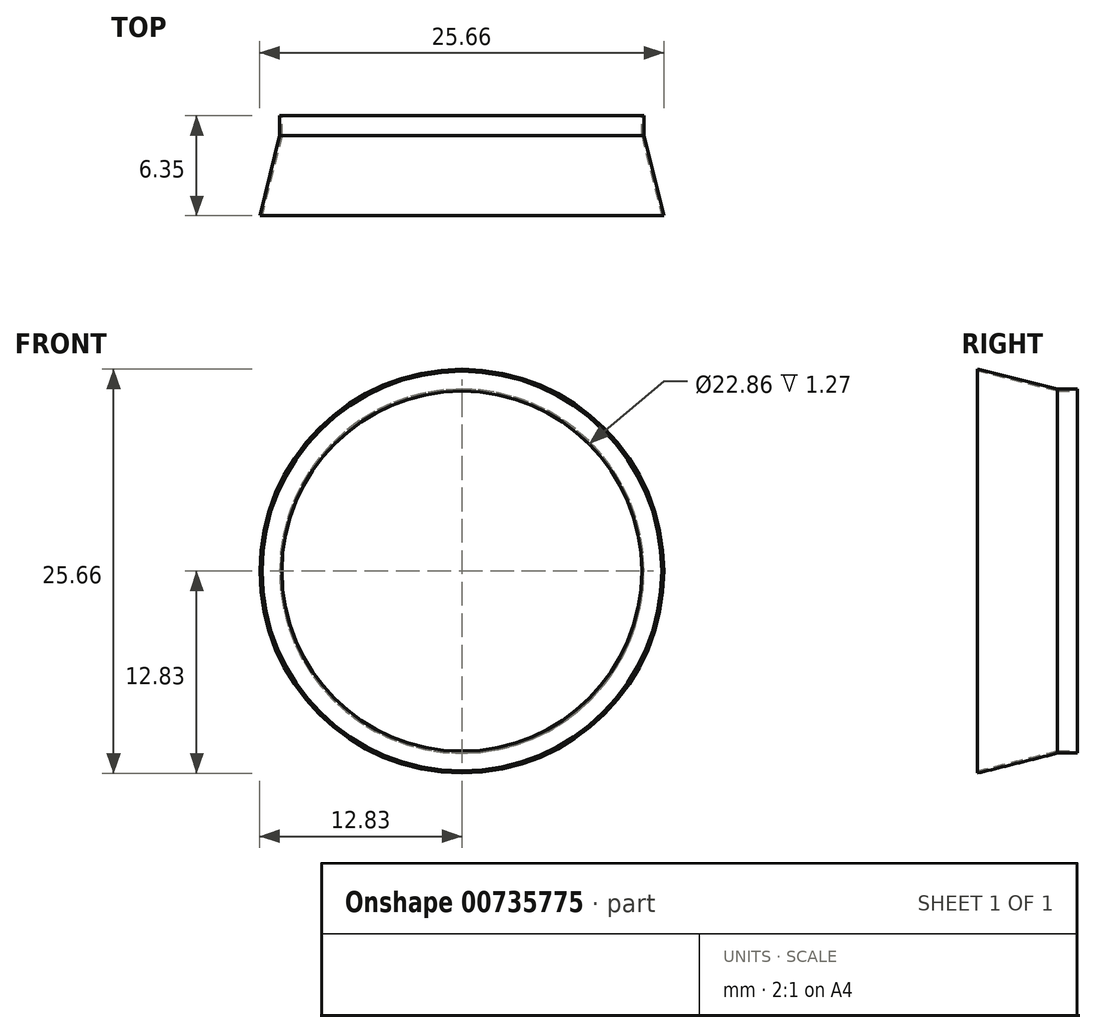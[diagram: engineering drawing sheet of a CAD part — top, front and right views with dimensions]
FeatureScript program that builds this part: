
annotation { "Feature Type Name" : "Feature", "Feature Type Description" : "" }
export const myFeature = defineFeature(function(context is Context, id is Id, definition is map)
    precondition{}
    {
        {
            var Q0;
            Q0=qCreatedBy(makeId("Top.planeOp"),FACE);
            var sketch = newSketch(context, id + "F0", { "sketchPlane" : qUnion([Q0])});
            skLineSegment(sketch, "E0", {"start": v(11.43, 66.28) * mm, "end": v(12.7, 61.2) * mm});
            skLineSegment(sketch, "E1", {"start": v(11.43, 66.28) * mm, "end": v(0, 66.28) * mm});
            skLineSegment(sketch, "E2", {"start": v(12.7, 61.2) * mm, "end": v(0, 61.2) * mm});
            skLineSegment(sketch, "E3", {"start": v(0, 61.2) * mm, "end": v(0, 66.28) * mm});
            skLineSegment(sketch, "E4", {"start": v(11.43, 66.28) * mm, "end": v(11.56, 66.28) * mm});
            skLineSegment(sketch, "E5", {"start": v(12.7, 61.2) * mm, "end": v(12.83, 61.2) * mm});
            skLineSegment(sketch, "E6", {"start": v(11.56, 66.28) * mm, "end": v(12.83, 61.2) * mm});
            skLineSegment(sketch, "E7", {"start": v(11.56, 66.28) * mm, "end": v(11.56, 67.55) * mm});
            skLineSegment(sketch, "E8", {"start": v(11.56, 67.55) * mm, "end": v(0, 67.55) * mm});
            skLineSegment(sketch, "E9", {"start": v(0, 67.55) * mm, "end": v(0, 66.28) * mm});
            skLineSegment(sketch, "E10", {"start": v(11.43, 66.28) * mm, "end": v(11.43, 67.55) * mm});
            skLineSegment(sketch, "E11", {"start": v(11.43, 67.55) * mm, "end": v(11.56, 67.55) * mm});
            skSolve(sketch);
        }
        {
            var Q0;
            Q0=makeQuery(id+"F0.imprint","IMPRINT",FACE,{"disambiguationData":[TD([[makeQuery(id+"F0.imprint","IMPRINT",EDGE,{"derivedFrom":sQuery(id+"F0.wireOp",EDGE,"E0")}),1.0]])]});
            var Q1;
            Q1=sQuery(id+"F0.wireOp",EDGE,"E3");
            revolve(context, id + "F1", {"surfaceOperationType" : NewSurfaceOperationType.NEW, "entities" : qUnion([Q0]), "axis" : qUnion([Q1]), "revolveType" : RevolveType.FULL});
        }
        {
            var Q0;
            Q0=makeQuery(id+"F0.imprint","IMPRINT",FACE,{"disambiguationData":[TD([[makeQuery(id+"F0.imprint","IMPRINT",EDGE,{"derivedFrom":sQuery(id+"F0.wireOp",EDGE,"E4")}),1.0]])]});
            var Q1;
            Q1=sQuery(id+"F0.wireOp",EDGE,"E9");
            revolve(context, id + "F2", {"operationType" : NewBodyOperationType.ADD, "surfaceOperationType" : NewSurfaceOperationType.NEW, "entities" : qUnion([Q0]), "axis" : qUnion([Q1]), "revolveType" : RevolveType.FULL});
        }
    });
